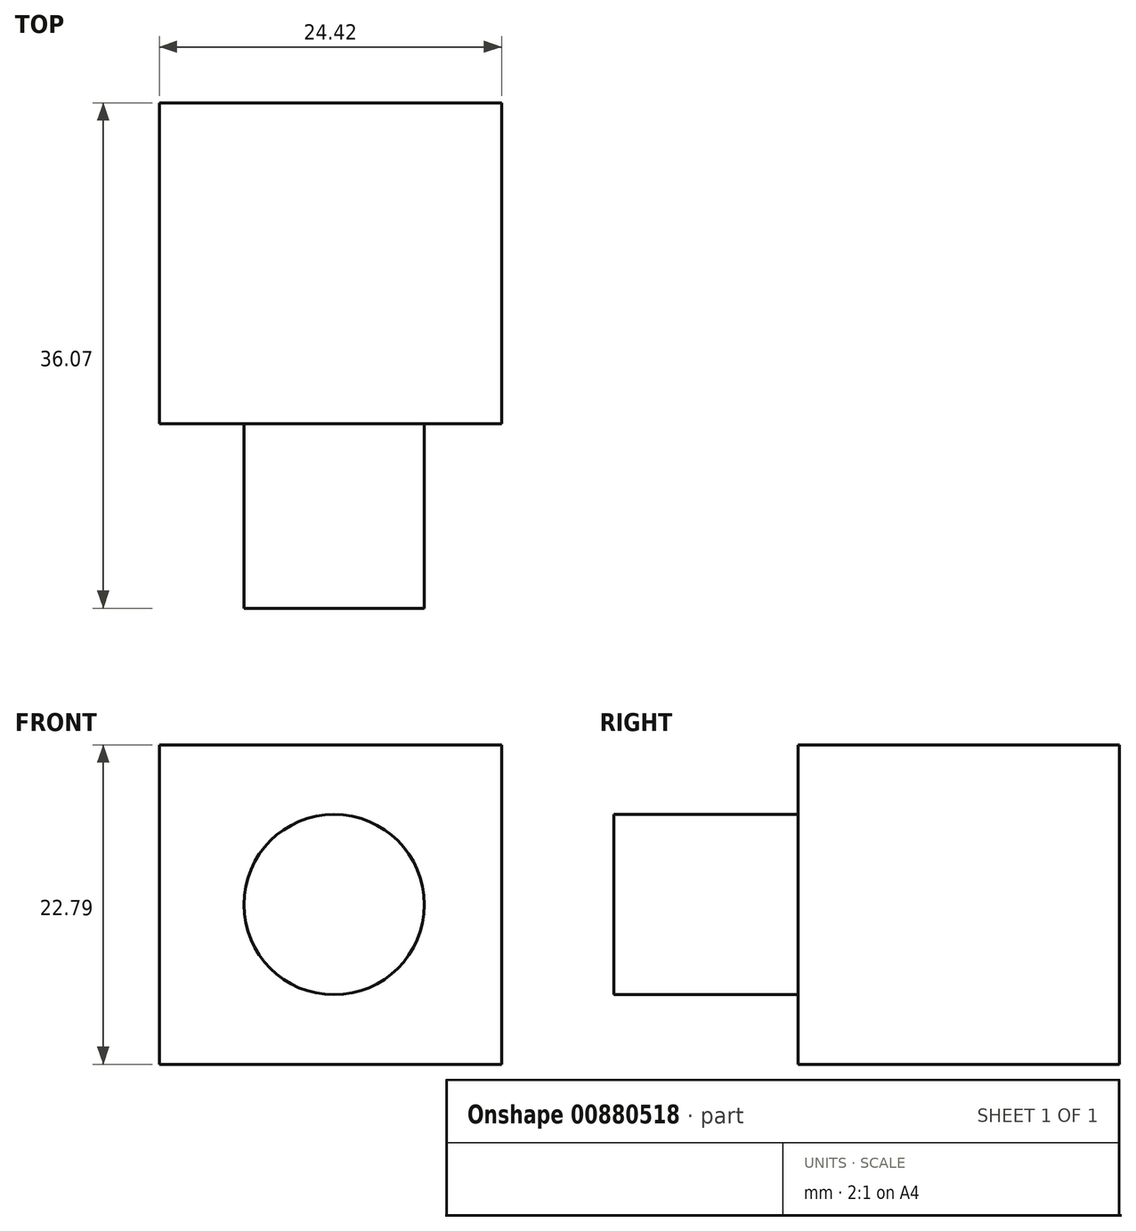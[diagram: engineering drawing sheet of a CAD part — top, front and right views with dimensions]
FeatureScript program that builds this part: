
annotation { "Feature Type Name" : "Feature", "Feature Type Description" : "" }
export const myFeature = defineFeature(function(context is Context, id is Id, definition is map)
    precondition{}
    {
        {
            var Q0;
            Q0=qCreatedBy(makeId("Front.planeOp"),FACE);
            var sketch = newSketch(context, id + "F0", { "sketchPlane" : qUnion([Q0])});
            skLineSegment(sketch, "E0.bottom", {"start": v(0, 0) * mm, "end": v(22.05, 0) * mm});
            skLineSegment(sketch, "E0.top", {"start": v(0, -22.8) * mm, "end": v(22.05, -22.8) * mm});
            skLineSegment(sketch, "E0.left", {"start": v(0, 0) * mm, "end": v(0, -22.8) * mm});
            skLineSegment(sketch, "E0.right", {"start": v(22.05, 0) * mm, "end": v(22.05, -22.8) * mm});
            skCircle(sketch, "E1", {"center": v(11.4, -9.8) * mm, "radius": 6.58 * mm});
            skCircle(sketch, "E2", {"center": v(34.52, -11.4) * mm, "radius": 6.44 * mm});
            skPoint(sketch, "E2.centerSnap0", {"position": v(22.05, -11.4) * mm});
            skLineSegment(sketch, "E3.bottom", {"start": v(22.05, 0) * mm, "end": v(46.47, 0) * mm});
            skLineSegment(sketch, "E3.top", {"start": v(22.05, -22.8) * mm, "end": v(46.47, -22.8) * mm});
            skLineSegment(sketch, "E3.right", {"start": v(46.47, 0) * mm, "end": v(46.47, -22.8) * mm});
            skSolve(sketch);
        }
        {
            var Q0;
            Q0=makeQuery(id+"F0.imprint","IMPRINT",FACE,{"disambiguationData":[TD([[makeQuery(id+"F0.imprint","IMPRINT",EDGE,{"derivedFrom":sQuery(id+"F0.wireOp",EDGE,"E2")}),1.0]])]});
            extrude(context, id + "F1", {"entities" : qUnion([Q0]), "depth" : 36.07 * mm, "offsetDistance" : 25.4 * mm});
        }
        {
            var Q0;
            Q0=makeQuery(id+"F0.imprint","IMPRINT",FACE,{"disambiguationData":[TD([[makeQuery(id+"F0.imprint","IMPRINT",EDGE,{"derivedFrom":sQuery(id+"F0.wireOp",EDGE,"E2")}),-1.0]])]});
            extrude(context, id + "F2", {"entities" : qUnion([Q0]), "operationType" : NewBodyOperationType.ADD, "depth" : 22.91 * mm, "offsetDistance" : 25.4 * mm});
        }
    });
